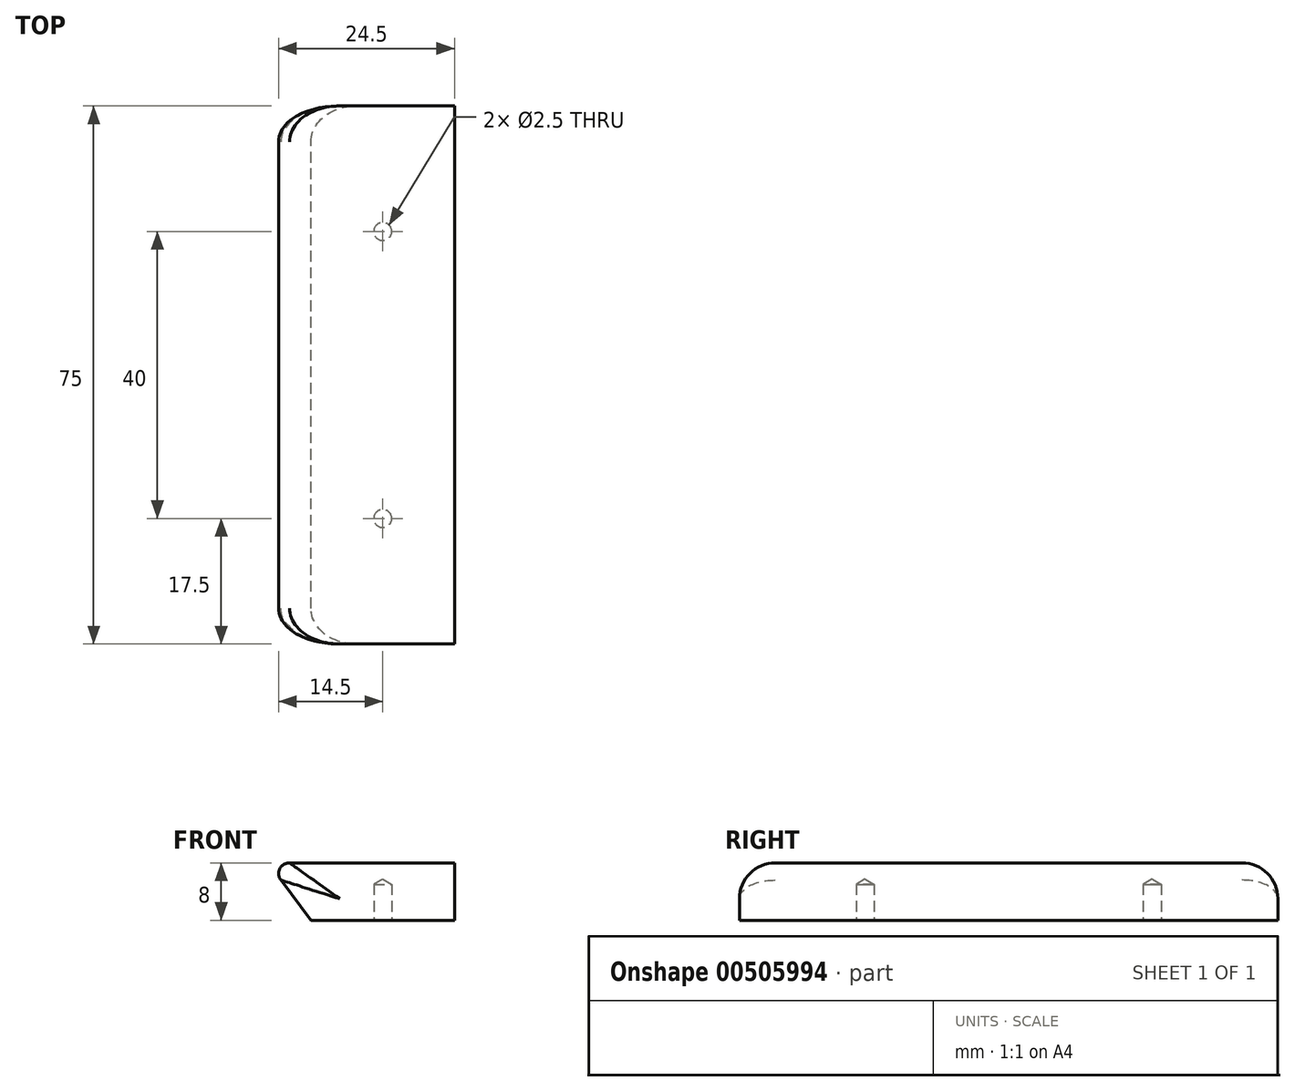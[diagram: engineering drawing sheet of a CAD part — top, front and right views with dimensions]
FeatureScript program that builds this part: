
annotation { "Feature Type Name" : "Feature", "Feature Type Description" : "" }
export const myFeature = defineFeature(function(context is Context, id is Id, definition is map)
    precondition{}
    {
        {
            var Q0;
            Q0=qCreatedBy(makeId("Front.planeOp"),FACE);
            var sketch = newSketch(context, id + "F0", { "sketchPlane" : qUnion([Q0])});
            skLineSegment(sketch, "E0", {"start": v(0, 0) * mm, "end": v(-20, 0) * mm});
            skLineSegment(sketch, "E1", {"start": v(-20, 0) * mm, "end": v(-24.2, 5.6) * mm});
            skLineSegment(sketch, "E2", {"start": v(-23, 8) * mm, "end": v(0, 8) * mm});
            skLineSegment(sketch, "E3", {"start": v(0, 8) * mm, "end": v(0, 0) * mm});
            skPoint(sketch, "E4.visualSharp", {"position": v(-26, 8) * mm});
            skArc(sketch, "E4.filletArc", {"start": v(-23, 8) * mm, "mid": v(-24.34, 7.17) * mm, "end": v(-24.2, 5.6) * mm});
            skSolve(sketch);
        }
        {
            var Q0;
            Q0=makeQuery(id+"F0.imprint","IMPRINT",FACE,{"disambiguationData":[TD([[makeQuery(id+"F0.imprint","IMPRINT",EDGE,{"derivedFrom":sQuery(id+"F0.wireOp",EDGE,"E0")}),-1.0]])]});
            extrude(context, id + "F1", {"entities" : qUnion([Q0]), "depth" : 75 * mm, "offsetDistance" : 25 * mm});
        }
        {
            var Q0;
            Q0=makeQuery(id+"F1.opExtrude","CAP_EDGE",EDGE,{"disambiguationData":[OSD([sQuery(id+"F0.wireOp",EDGE,"E2")])],"isStart":false});
            var Q1;
            Q1=makeQuery(id+"F1.opExtrude","CAP_EDGE",EDGE,{"disambiguationData":[OSD([sQuery(id+"F0.wireOp",EDGE,"E2")])],"isStart":true});
            fillet(context, id + "F2", {"entities" : qUnion([Q0, Q1]), "radius" : 5 * mm, "tangentPropagation" : true, "allowEdgeOverflow" : false});
        }
        {
            var Q0;
            Q0=makeQuery(id+"F1.opExtrude","SWEPT_FACE",FACE,{"disambiguationData":[OSD([sQuery(id+"F0.wireOp",EDGE,"E0")])]});
            var sketch = newSketch(context, id + "F3", { "sketchPlane" : qUnion([Q0])});
            skPoint(sketch, "E5", {"position": v(-10, 57.5) * mm});
            skPoint(sketch, "E6", {"position": v(-10, 17.5) * mm});
            skSolve(sketch);
        }
        {
            var Q0;
            Q0=sQuery(id+"F3.wireOp",VERTEX,"E5");
            var Q1;
            Q1=sQuery(id+"F3.wireOp",VERTEX,"E6");
            var Q2;
            Q2=makeQuery(id+"F1.opExtrude","SWEPT_BODY",BODY,{"disambiguationData":[OSD([sQuery(id+"F0.wireOp",EDGE,"E0"),sQuery(id+"F0.wireOp",EDGE,"E1"),sQuery(id+"F0.wireOp",EDGE,"E2"),sQuery(id+"F0.wireOp",EDGE,"E3"),sQuery(id+"F0.wireOp",EDGE,"E4.filletArc")])]});
            hole(context, id + "F4", {"style" : HoleStyle.SIMPLE, "endStyle" : HoleEndStyle.BLIND, "holeDiameter" : 2.5 * mm, "holeDepth" : 5 * mm, "isTappedThrough" : true, "tappedDepth" : 12 * mm, "tapClearance" : 3, "locations" : qUnion([Q0, Q1]), "scope" : qUnion([Q2])});
        }
    });
